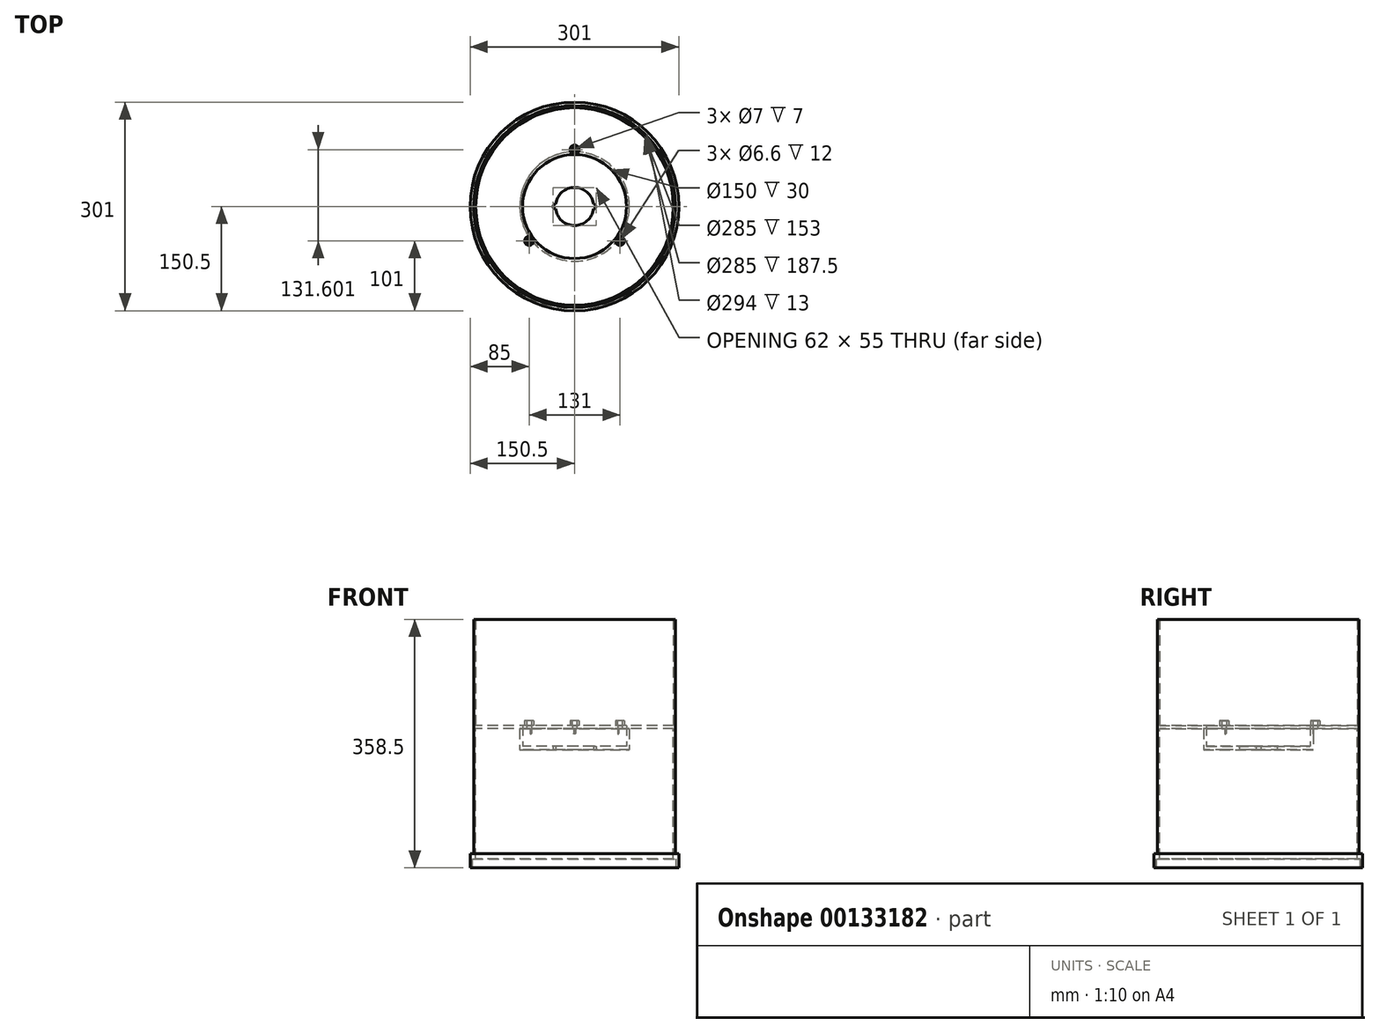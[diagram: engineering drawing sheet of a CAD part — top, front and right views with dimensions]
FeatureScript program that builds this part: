
annotation { "Feature Type Name" : "Feature", "Feature Type Description" : "" }
export const myFeature = defineFeature(function(context is Context, id is Id, definition is map)
    precondition{}
    {
        {
            var Q0;
            Q0=qCreatedBy(makeId("Top.planeOp"),FACE);
            var sketch = newSketch(context, id + "F0", { "sketchPlane" : qUnion([Q0])});
            skCircle(sketch, "E0", {"center": v(0, 0) * mm, "radius": 79 * mm});
            skArc(sketch, "E1", {"start": v(27.28, 3.5) * mm, "mid": v(0, 27.5) * mm, "end": v(-27.28, 3.5) * mm});
            skArc(sketch, "E2", {"start": v(-27.28, 3.5) * mm, "mid": v(-31, 0) * mm, "end": v(-27.28, -3.5) * mm});
            skArc(sketch, "E3", {"start": v(27.28, -3.5) * mm, "mid": v(31, 0) * mm, "end": v(27.28, 3.5) * mm});
            skArc(sketch, "E4.trimOffspring", {"start": v(-27.28, -3.5) * mm, "mid": v(0, -27.5) * mm, "end": v(27.28, -3.5) * mm});
            skCircle(sketch, "E5", {"center": v(0, 0) * mm, "radius": 75 * mm});
            skSolve(sketch);
        }
        {
            var Q0;
            Q0=makeQuery(id+"F0.imprint","IMPRINT",FACE,{"disambiguationData":[TD([[makeQuery(id+"F0.imprint","IMPRINT",EDGE,{"derivedFrom":sQuery(id+"F0.wireOp",EDGE,"E1")}),-1.0]])]});
            extrude(context, id + "F1", {"entities" : qUnion([Q0]), "depth" : 5 * mm});
        }
        {
            var Q0;
            Q0=makeQuery(id+"F0.imprint","IMPRINT",FACE,{"disambiguationData":[TD([[makeQuery(id+"F0.imprint","IMPRINT",EDGE,{"derivedFrom":sQuery(id+"F0.wireOp",EDGE,"E0")}),1.0]])]});
            extrude(context, id + "F2", {"entities" : qUnion([Q0]), "operationType" : NewBodyOperationType.ADD, "depth" : 30 * mm});
        }
        {
            var Q0;
            Q0=makeQuery(id+"F2.opExtrude","CAP_FACE",FACE,{"disambiguationData":[OSD([sQuery(id+"F0.wireOp",EDGE,"E0"),sQuery(id+"F0.wireOp",EDGE,"E5")])],"isStart":false});
            var sketch = newSketch(context, id + "F3", { "sketchPlane" : qUnion([Q0])});
            skCircle(sketch, "E6", {"center": v(0, 0) * mm, "radius": 142.5 * mm});
            skCircle(sketch, "E7.0", {"center": v(0, 0) * mm, "radius": 145.5 * mm});
            skSolve(sketch);
        }
        {
            var Q0;
            Q0=makeQuery(id+"F3.imprint","IMPRINT",FACE,{"disambiguationData":[TD([[makeQuery(id+"F3.imprint","IMPRINT",EDGE,{"derivedFrom":sQuery(id+"F3.wireOp",EDGE,"E6")}),1.0]])]});
            var Q1;
            Q1=makeQuery(id+"F3.imprint","IMPRINT",FACE,{"disambiguationData":[TD([[makeQuery(id+"F3.imprint","IMPRINT",EDGE,{"derivedFrom":makeQuery(id+"F2.opExtrude","CAP_EDGE",EDGE,{"disambiguationData":[OSD([sQuery(id+"F0.wireOp",EDGE,"E0")])],"isStart":false})}),1.0]])]});
            extrude(context, id + "F4", {"entities" : qUnion([Q0, Q1]), "operationType" : NewBodyOperationType.ADD, "depth" : 5 * mm});
        }
        {
            var Q0;
            Q0=makeQuery(id+"F3.imprint","IMPRINT",FACE,{"disambiguationData":[TD([[makeQuery(id+"F3.imprint","IMPRINT",EDGE,{"derivedFrom":sQuery(id+"F3.wireOp",EDGE,"E6")}),-1.0]])]});
            extrude(context, id + "F5", {"entities" : qUnion([Q0]), "operationType" : NewBodyOperationType.ADD, "depth" : 158 * mm});
        }
        {
            var Q0;
            Q0=makeQuery(id+"F3.imprint","IMPRINT",FACE,{"disambiguationData":[TD([[makeQuery(id+"F3.imprint","IMPRINT",EDGE,{"derivedFrom":sQuery(id+"F3.wireOp",EDGE,"E6")}),-1.0]])]});
            extrude(context, id + "F6", {"entities" : qUnion([Q0]), "operationType" : NewBodyOperationType.ADD, "oppositeDirection" : true, "depth" : 180 * mm});
        }
        {
            var Q0;
            Q0=makeQuery(id+"F6.opExtrude","CAP_FACE",FACE,{"disambiguationData":[OSD([sQuery(id+"F3.wireOp",EDGE,"E6"),sQuery(id+"F3.wireOp",EDGE,"E7.0")])],"isStart":false});
            var sketch = newSketch(context, id + "F7", { "sketchPlane" : qUnion([Q0])});
            skCircle(sketch, "E8", {"center": v(0, 0) * mm, "radius": 150.5 * mm});
            skSolve(sketch);
        }
        {
            var Q0;
            Q0=makeQuery(id+"F7.imprint","IMPRINT",FACE,{"disambiguationData":[TD([[makeQuery(id+"F7.imprint","IMPRINT",EDGE,{"derivedFrom":sQuery(id+"F7.wireOp",EDGE,"E8")}),1.0]])]});
            var Q1;
            Q1=makeQuery(id+"F7.imprint","IMPRINT",FACE,{"disambiguationData":[TD([[makeQuery(id+"F7.imprint","IMPRINT",EDGE,{"derivedFrom":makeQuery(id+"F6.opExtrude","CAP_EDGE",EDGE,{"disambiguationData":[OSD([sQuery(id+"F3.wireOp",EDGE,"E6")])],"isStart":false})}),1.0]])]});
            extrude(context, id + "F8", {"entities" : qUnion([Q0, Q1]), "operationType" : NewBodyOperationType.ADD, "depth" : 7.5 * mm});
        }
        {
            var Q0;
            Q0=makeQuery(id+"F8.opExtrude","CAP_FACE",FACE,{"disambiguationData":[OSD([sQuery(id+"F3.wireOp",EDGE,"E6"),sQuery(id+"F7.wireOp",EDGE,"E8")])],"isStart":false});
            var sketch = newSketch(context, id + "F9", { "sketchPlane" : qUnion([Q0])});
            skCircle(sketch, "E9", {"center": v(0, 0) * mm, "radius": 147 * mm});
            skSolve(sketch);
        }
        {
            var Q0;
            Q0=makeQuery(id+"F9.imprint","IMPRINT",FACE,{"disambiguationData":[TD([[makeQuery(id+"F9.imprint","IMPRINT",EDGE,{"derivedFrom":sQuery(id+"F9.wireOp",EDGE,"E9")}),-1.0]])]});
            extrude(context, id + "F10", {"entities" : qUnion([Q0]), "operationType" : NewBodyOperationType.ADD, "depth" : 13 * mm});
        }
        {
            var Q0;
            Q0=makeQuery(id+"F4.opExtrude","CAP_FACE",FACE,{"disambiguationData":[OSD([sQuery(id+"F0.wireOp",EDGE,"E5"),sQuery(id+"F3.wireOp",EDGE,"E6")])],"isStart":false});
            var sketch = newSketch(context, id + "F11", { "sketchPlane" : qUnion([Q0])});
            skCircle(sketch, "E10", {"center": v(0, 82.1) * mm, "radius": 6.5 * mm});
            skCircle(sketch, "E11", {"center": v(0, 82.1) * mm, "radius": 3.5 * mm});
            skLineSegment(sketch, "E12", {"start": v(0, 0) * mm, "end": v(0, 82.1) * mm, "construction": true});
            skCircle(sketch, "E13", {"center": v(0, 0) * mm, "radius": 82.1 * mm, "construction": true});
            skCircle(sketch, "E14", {"center": v(65.5, -49.5) * mm, "radius": 6.5 * mm});
            skCircle(sketch, "E15", {"center": v(65.5, -49.5) * mm, "radius": 3.5 * mm});
            skCircle(sketch, "E16", {"center": v(-65.5, -49.5) * mm, "radius": 6.5 * mm});
            skCircle(sketch, "E17", {"center": v(-65.5, -49.5) * mm, "radius": 3.5 * mm});
            skSolve(sketch);
        }
        {
            var Q0;
            Q0 = qSketchRegion(id + "F11", true);
            extrude(context, id + "F12", {"entities" : qUnion([Q0]), "operationType" : NewBodyOperationType.ADD, "depth" : 7 * mm});
        }
        {
            var Q0;
            Q0=sQuery(id+"F11.wireOp",VERTEX,"E11.center");
            var Q1;
            Q1=sQuery(id+"F11.wireOp",VERTEX,"E15.center");
            var Q2;
            Q2=sQuery(id+"F11.wireOp",VERTEX,"E17.center");
            var Q3;
            Q3=makeQuery(id+"F1.opExtrude","SWEPT_BODY",BODY,{"disambiguationData":[OSD([sQuery(id+"F0.wireOp",EDGE,"E1"),sQuery(id+"F0.wireOp",EDGE,"E2"),sQuery(id+"F0.wireOp",EDGE,"E3"),sQuery(id+"F0.wireOp",EDGE,"E4.trimOffspring"),sQuery(id+"F0.wireOp",EDGE,"E5")])]});
            hole(context, id + "F13", {"style" : HoleStyle.SIMPLE, "endStyle" : HoleEndStyle.BLIND, "standardTappedOrClearance" : lookupTablePath({ "standard" : "ISO", "fit" : "Normal", "size" : "M6", "type" : "Clearance" }), "standardBlindInLast" : lookupTablePath({ "fit" : "Standard", "standard" : "ISO", "size" : "M6", "type" : "Clearance" }), "holeDiameter" : 6.6 * mm, "holeDepth" : 12 * mm, "locations" : qUnion([Q0, Q1, Q2]), "scope" : qUnion([Q3]), "tappedDepth" : 12 * mm, "tapClearance" : 3, "startStyle" : HoleStartStyle.PART});
        }
    });
